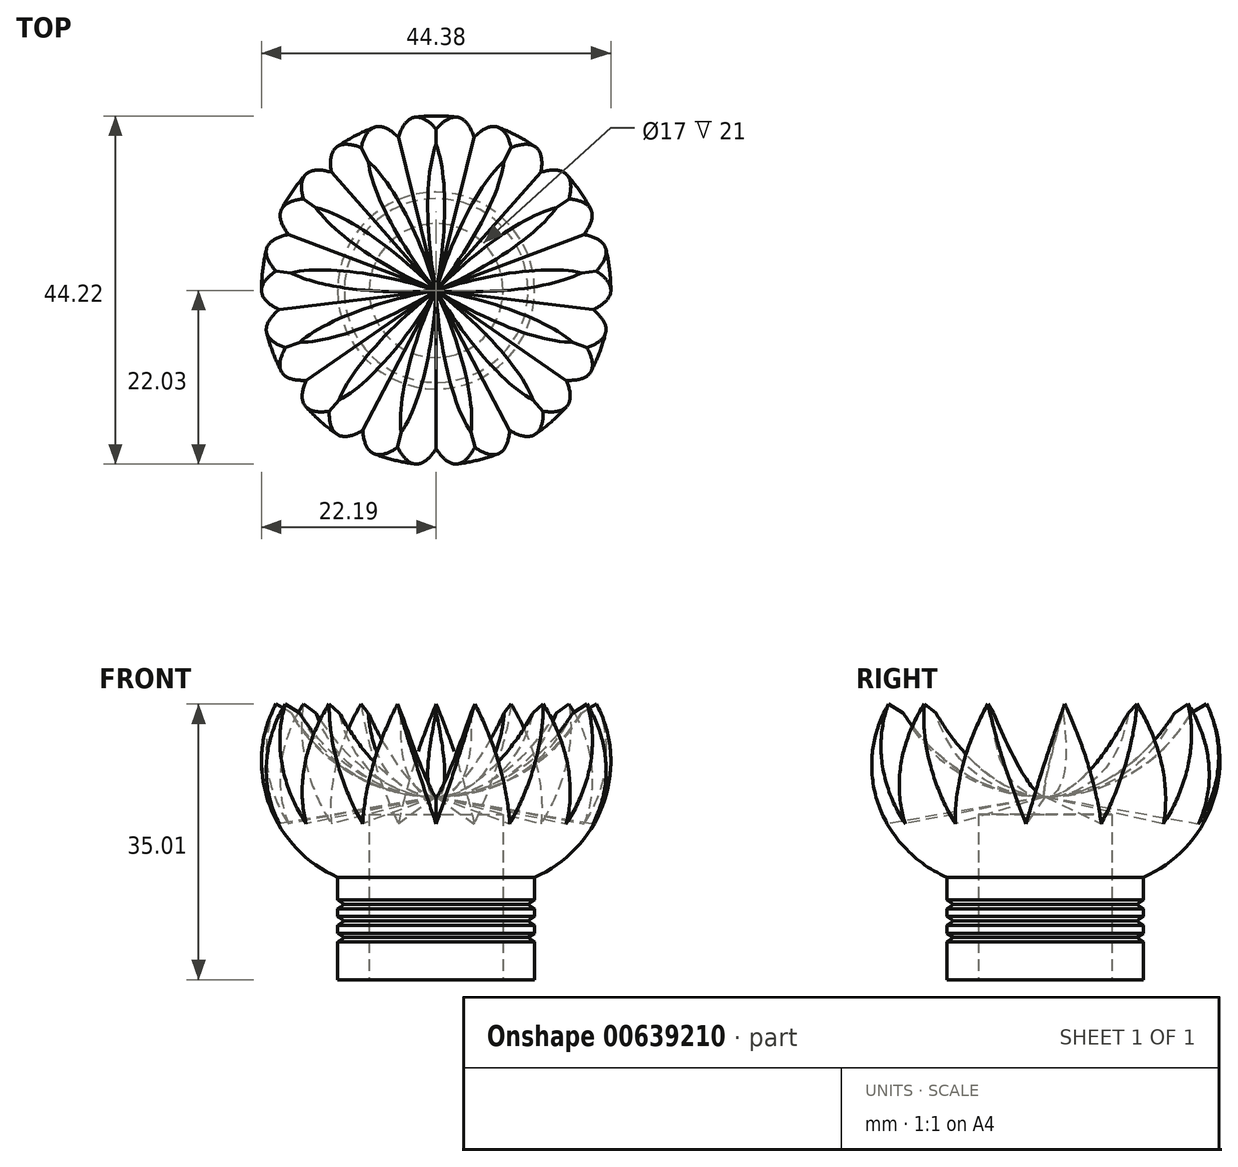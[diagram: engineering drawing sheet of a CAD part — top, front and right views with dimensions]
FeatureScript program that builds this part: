
annotation { "Feature Type Name" : "Feature", "Feature Type Description" : "" }
export const myFeature = defineFeature(function(context is Context, id is Id, definition is map)
    precondition{}
    {
        {
            var Q0;
            Q0=qCreatedBy(makeId("Front.planeOp"),FACE);
            var sketch = newSketch(context, id + "F0", { "sketchPlane" : qUnion([Q0])});
            skLineSegment(sketch, "E0", {"start": v(0, 0) * mm, "end": v(0, 21) * mm});
            skLineSegment(sketch, "E1", {"start": v(0, 21) * mm, "end": v(-8.5, 21) * mm});
            skLineSegment(sketch, "E2", {"start": v(-8.5, 0) * mm, "end": v(-12.5, 0) * mm});
            skLineSegment(sketch, "E3", {"start": v(-12.5, 0) * mm, "end": v(-12.5, 4.78) * mm});
            skArc(sketch, "E4", {"start": v(-20.33, 35.33) * mm, "mid": v(-21.27, 22.46) * mm, "end": v(-12.5, 13) * mm});
            skLineSegment(sketch, "E5", {"start": v(-20.33, 35.33) * mm, "end": v(-19.33, 35.33) * mm});
            skArc(sketch, "E6", {"start": v(-19.33, 35.33) * mm, "mid": v(-11.4, 26.5) * mm, "end": v(0, 23.21) * mm});
            skLineSegment(sketch, "E7", {"start": v(-12.5, 4.78) * mm, "end": v(-11.67, 5.34) * mm});
            skLineSegment(sketch, "E8", {"start": v(-11.67, 5.34) * mm, "end": v(-12.5, 5.9) * mm});
            skLineSegment(sketch, "E9", {"start": v(-12.5, 5.9) * mm, "end": v(-12.5, 6.9) * mm});
            skLineSegment(sketch, "E10", {"start": v(-12.5, 6.9) * mm, "end": v(-11.67, 7.45) * mm});
            skLineSegment(sketch, "E11", {"start": v(-11.67, 7.45) * mm, "end": v(-12.5, 8.01) * mm});
            skLineSegment(sketch, "E12", {"start": v(-12.5, 8.01) * mm, "end": v(-12.5, 9) * mm});
            skLineSegment(sketch, "E13", {"start": v(-12.5, 9) * mm, "end": v(-11.67, 9.57) * mm});
            skLineSegment(sketch, "E14", {"start": v(-11.67, 9.57) * mm, "end": v(-12.5, 10.13) * mm});
            skLineSegment(sketch, "E15", {"start": v(-12.5, 10.13) * mm, "end": v(-12.5, 11.12) * mm});
            skLineSegment(sketch, "E16", {"start": v(-8.5, 21) * mm, "end": v(-8.5, 0) * mm});
            skLineSegment(sketch, "E17.trimOffspring", {"start": v(-12.5, 10.13) * mm, "end": v(-12.5, 13) * mm});
            skLineSegment(sketch, "E18", {"start": v(0, 23.21) * mm, "end": v(0, 21) * mm});
            skSolve(sketch);
        }
        {
            var Q0;
            Q0=makeQuery(id+"F0.imprint","IMPRINT",FACE,{"disambiguationData":[TD([[makeQuery(id+"F0.imprint","IMPRINT",EDGE,{"derivedFrom":sQuery(id+"F0.wireOp",EDGE,"E1")}),-1.0]])]});
            var Q1;
            Q1=sQuery(id+"F0.wireOp",EDGE,"E0");
            revolve(context, id + "F1", {"entities" : qUnion([Q0]), "axis" : qUnion([Q1]), "revolveType" : RevolveType.FULL});
        }
        {
            var Q0;
            Q0=qCreatedBy(makeId("Front.planeOp"),FACE);
            var sketch = newSketch(context, id + "F2", { "sketchPlane" : qUnion([Q0])});
            skLineSegment(sketch, "E19", {"start": v(0, 35.6) * mm, "end": v(4, 35.6) * mm});
            skLineSegment(sketch, "E20", {"start": v(4, 35.6) * mm, "end": v(0, 23.23) * mm});
            skLineSegment(sketch, "E21.MirrorCS", {"start": v(0, 35.6) * mm, "end": v(-4, 35.6) * mm});
            skLineSegment(sketch, "E22.MirrorCS", {"start": v(-4, 35.6) * mm, "end": v(0, 23.23) * mm});
            skSolve(sketch);
        }
        {
            var Q0;
            Q0=qSketchRegion(id+"F2",true);
            extrude(context, id + "F3", {"entities" : qUnion([Q0]), "endBound" : BoundingType.THROUGH_ALL, "depth" : 25 * mm, "offsetDistance" : 25 * mm, "hasDraft" : true, "draftAngle" : 3 * degree});
        }
        {
            var Q0;
            Q0=makeQuery(id+"F3.opExtrude","SWEPT_BODY",BODY,{"disambiguationData":[OSD([sQuery(id+"F2.wireOp",EDGE,"E19"),sQuery(id+"F2.wireOp",EDGE,"E20"),sQuery(id+"F2.wireOp",EDGE,"427e0060-5137-45d8-8873-1bbb9a4445e30.MirrorCS"),sQuery(id+"F2.wireOp",EDGE,"36f27a8a-8354-4016-83d8-3e2d0c1ddbe20.MirrorCS")])]});
            var Q1;
            Q1=makeQuery(id+"F1.opRevolve","SWEPT_FACE",FACE,{"disambiguationData":[OSD([sQuery(id+"F0.wireOp",EDGE,"E17.trimOffspring")])]});
            circularPattern(context, id + "F4", {"operationType" : NewBodyOperationType.REMOVE, "entities" : qUnion([Q0]), "axis" : qUnion([Q1]), "angle" : 360 * degree, "instanceCount" : 13, "equalSpace" : true});
        }
    });
